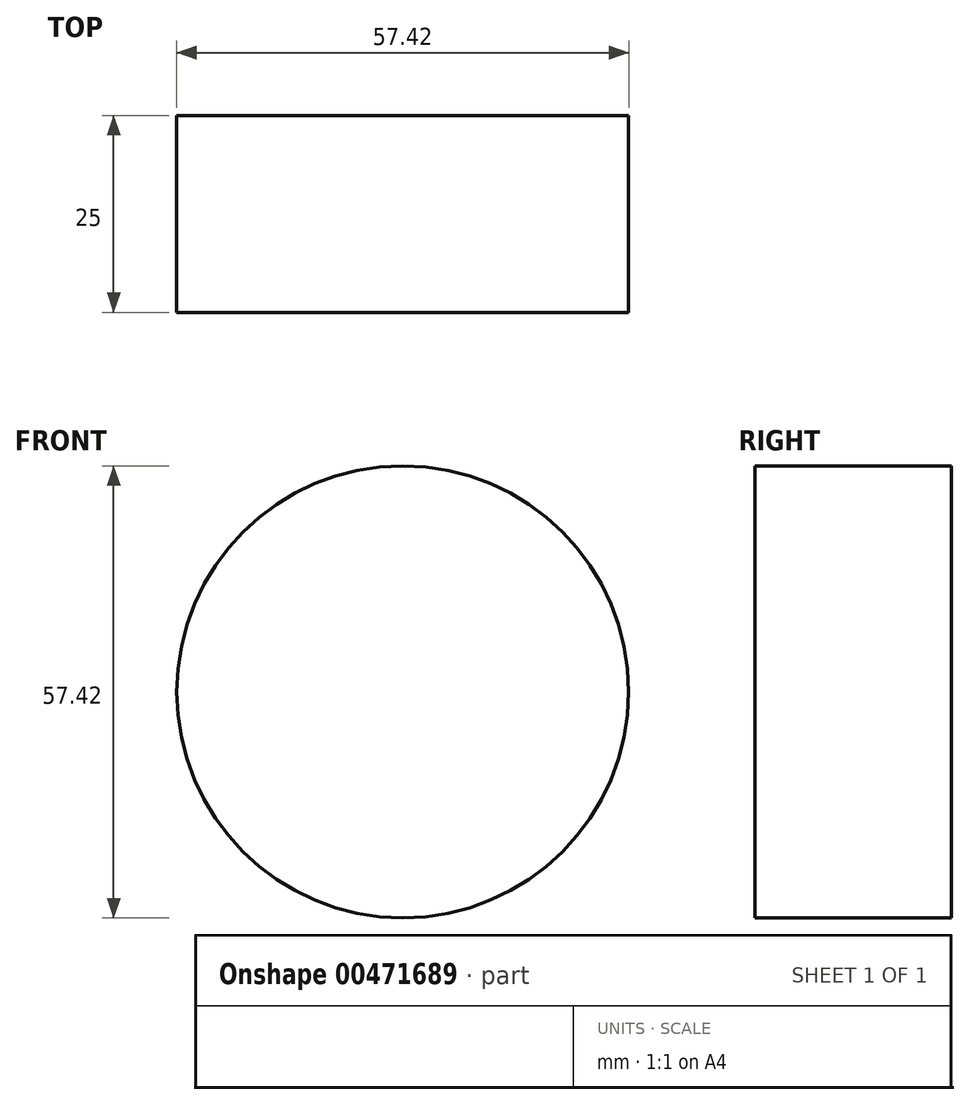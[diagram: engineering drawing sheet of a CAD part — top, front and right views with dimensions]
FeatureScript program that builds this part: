
annotation { "Feature Type Name" : "Feature", "Feature Type Description" : "" }
export const myFeature = defineFeature(function(context is Context, id is Id, definition is map)
    precondition{}
    {
        {
            var Q0;
            Q0=qCreatedBy(makeId("Front.planeOp"),FACE);
            var sketch = newSketch(context, id + "F0", { "sketchPlane" : qUnion([Q0])});
            skCircle(sketch, "E0", {"center": v(0, 0) * mm, "radius": 28.7 * mm});
            skSolve(sketch);
        }
        {
            var Q0;
            Q0=makeQuery(id+"F0.imprint","IMPRINT",FACE,{"disambiguationData":[TD([[makeQuery(id+"F0.imprint","IMPRINT",EDGE,{"derivedFrom":sQuery(id+"F0.wireOp",EDGE,"E0")}),1.0]])]});
            extrude(context, id + "F1", {"entities" : qUnion([Q0]), "depth" : 25 * mm});
        }
    });
